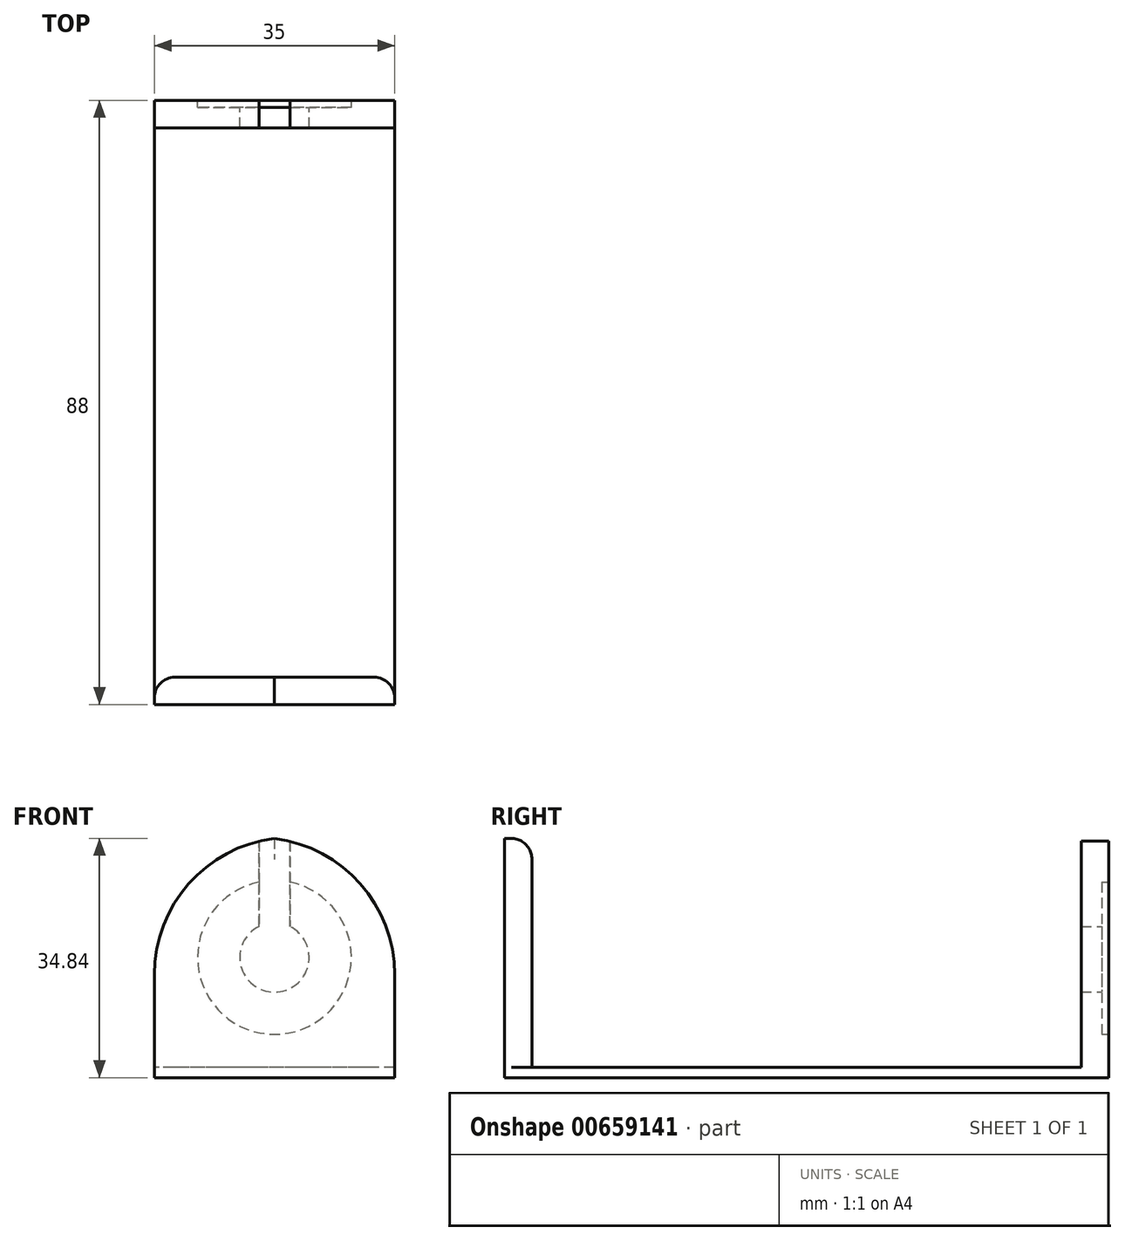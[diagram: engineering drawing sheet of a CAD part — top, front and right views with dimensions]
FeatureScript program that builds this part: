
annotation { "Feature Type Name" : "Feature", "Feature Type Description" : "" }
export const myFeature = defineFeature(function(context is Context, id is Id, definition is map)
    precondition{}
    {
        {
            var Q0;
            Q0=qCreatedBy(makeId("Right.planeOp"),FACE);
            var sketch = newSketch(context, id + "F0", { "sketchPlane" : qUnion([Q0])});
            skLineSegment(sketch, "E0", {"start": v(-44, 0) * mm, "end": v(44, 0) * mm});
            skLineSegment(sketch, "E1", {"start": v(-44, 0) * mm, "end": v(-44, 35) * mm});
            skLineSegment(sketch, "E2", {"start": v(-44, 35) * mm, "end": v(-40, 35) * mm});
            skLineSegment(sketch, "E3", {"start": v(-40, 1.5) * mm, "end": v(40, 1.5) * mm});
            skLineSegment(sketch, "E4", {"start": v(40, 1.5) * mm, "end": v(40, 35) * mm});
            skLineSegment(sketch, "E5", {"start": v(40, 35) * mm, "end": v(44, 35) * mm});
            skLineSegment(sketch, "E6", {"start": v(44, 35) * mm, "end": v(44, 0) * mm});
            skLineSegment(sketch, "E7", {"start": v(-40, 35) * mm, "end": v(-40, 1.5) * mm});
            skSolve(sketch);
        }
        {
            var Q0;
            Q0=makeQuery(id+"F0.imprint","IMPRINT",FACE,{"disambiguationData":[TD([[makeQuery(id+"F0.imprint","IMPRINT",EDGE,{"derivedFrom":sQuery(id+"F0.wireOp",EDGE,"E0")}),1.0]])]});
            extrude(context, id + "F1", {"entities" : qUnion([Q0]), "endBound" : BoundingType.SYMMETRIC, "depth" : 35 * mm, "offsetDistance" : 25 * mm});
        }
        {
            var Q0;
            Q0=makeQuery(id+"F1.opExtrude","CAP_EDGE",EDGE,{"disambiguationData":[OSD([sQuery(id+"F0.wireOp",EDGE,"E5")])],"isStart":false});
            var Q1;
            Q1=makeQuery(id+"F1.opExtrude","CAP_EDGE",EDGE,{"disambiguationData":[OSD([sQuery(id+"F0.wireOp",EDGE,"E5")])],"isStart":true});
            var Q2;
            Q2=makeQuery(id+"F1.opExtrude","CAP_EDGE",EDGE,{"disambiguationData":[OSD([sQuery(id+"F0.wireOp",EDGE,"E2")])],"isStart":true});
            var Q3;
            Q3=makeQuery(id+"F1.opExtrude","CAP_EDGE",EDGE,{"disambiguationData":[OSD([sQuery(id+"F0.wireOp",EDGE,"E2")])],"isStart":false});
            fillet(context, id + "F2", {"entities" : qUnion([Q0, Q1, Q2, Q3]), "radius" : 20 * mm, "tangentPropagation" : true, "allowEdgeOverflow" : false});
        }
        {
            var Q0;
            Q0=makeQuery(id+"F1.opExtrude","SWEPT_FACE",FACE,{"disambiguationData":[OSD([sQuery(id+"F0.wireOp",EDGE,"E6")])]});
            var sketch = newSketch(context, id + "F3", { "sketchPlane" : qUnion([Q0])});
            skCircle(sketch, "E8", {"center": v(0, 17.5) * mm, "radius": 11.2 * mm});
            skArc(sketch, "E9", {"start": v(-2.25, 22.03) * mm, "mid": v(0, 12.46) * mm, "end": v(2.25, 22.03) * mm});
            skLineSegment(sketch, "E10", {"start": v(-2.25, 22.03) * mm, "end": v(-2.25, 39.22) * mm});
            skLineSegment(sketch, "E11", {"start": v(-2.25, 39.22) * mm, "end": v(2.25, 39.22) * mm});
            skPoint(sketch, "E12", {"position": v(0, 39.22) * mm});
            skLineSegment(sketch, "E13", {"start": v(2.25, 39.22) * mm, "end": v(2.25, 22.03) * mm});
            skSolve(sketch);
        }
        {
            var Q0;
            Q0=makeQuery(id+"F3.imprint","IMPRINT",FACE,{"disambiguationData":[TD([[makeQuery(id+"F3.imprint","IMPRINT",EDGE,{"derivedFrom":sQuery(id+"F3.wireOp",EDGE,"E8")}),1.0]])]});
            var Q1;
            Q1=makeQuery(id+"F3.imprint","IMPRINT",FACE,{"disambiguationData":[TD([[makeQuery(id+"F3.imprint","IMPRINT",EDGE,{"derivedFrom":sQuery(id+"F3.wireOp",EDGE,"E9")}),1.0]])]});
            extrude(context, id + "F4", {"entities" : qUnion([Q0, Q1]), "operationType" : NewBodyOperationType.REMOVE, "oppositeDirection" : true, "depth" : 1 * mm, "offsetDistance" : 25 * mm});
        }
        {
            var Q0;
            Q0=makeQuery(id+"F3.imprint","IMPRINT",FACE,{"disambiguationData":[TD([[makeQuery(id+"F3.imprint","IMPRINT",EDGE,{"derivedFrom":sQuery(id+"F3.wireOp",EDGE,"E9")}),1.0]])]});
            var Q1;
            {var subQ1=sQuery(id+"F3.wireOp",EDGE,"E8");var subQ9=sQuery(id+"F3.wireOp",EDGE,"E10");var subQ10=makeQuery(id+"F3.imprint","INTERSECT",VERTEX,{"derivedFrom":[subQ1,subQ9]});Q1=makeQuery(id+"F3.imprint","IMPRINT",FACE,{"disambiguationData":[TD([[makeQuery(id+"F3.imprint","IMPRINT",EDGE,{"disambiguationData":[TD([[subQ10,1.0]])],"derivedFrom":subQ1}),-1.0]])]});}
            extrude(context, id + "F5", {"entities" : qUnion([Q0, Q1]), "operationType" : NewBodyOperationType.REMOVE, "oppositeDirection" : true, "depth" : 25 * mm, "offsetDistance" : 25 * mm});
        }
        {
            var Q0;
            Q0=makeQuery(id+"F1.opExtrude","CAP_EDGE",EDGE,{"disambiguationData":[OSD([sQuery(id+"F0.wireOp",EDGE,"E7")])],"isStart":false});
            var Q1;
            Q1=makeQuery(id+"F1.opExtrude","CAP_EDGE",EDGE,{"disambiguationData":[OSD([sQuery(id+"F0.wireOp",EDGE,"E7")])],"isStart":true});
            fillet(context, id + "F6", {"entities" : qUnion([Q0, Q1]), "radius" : 3 * mm, "tangentPropagation" : true, "allowEdgeOverflow" : false});
        }
    });
